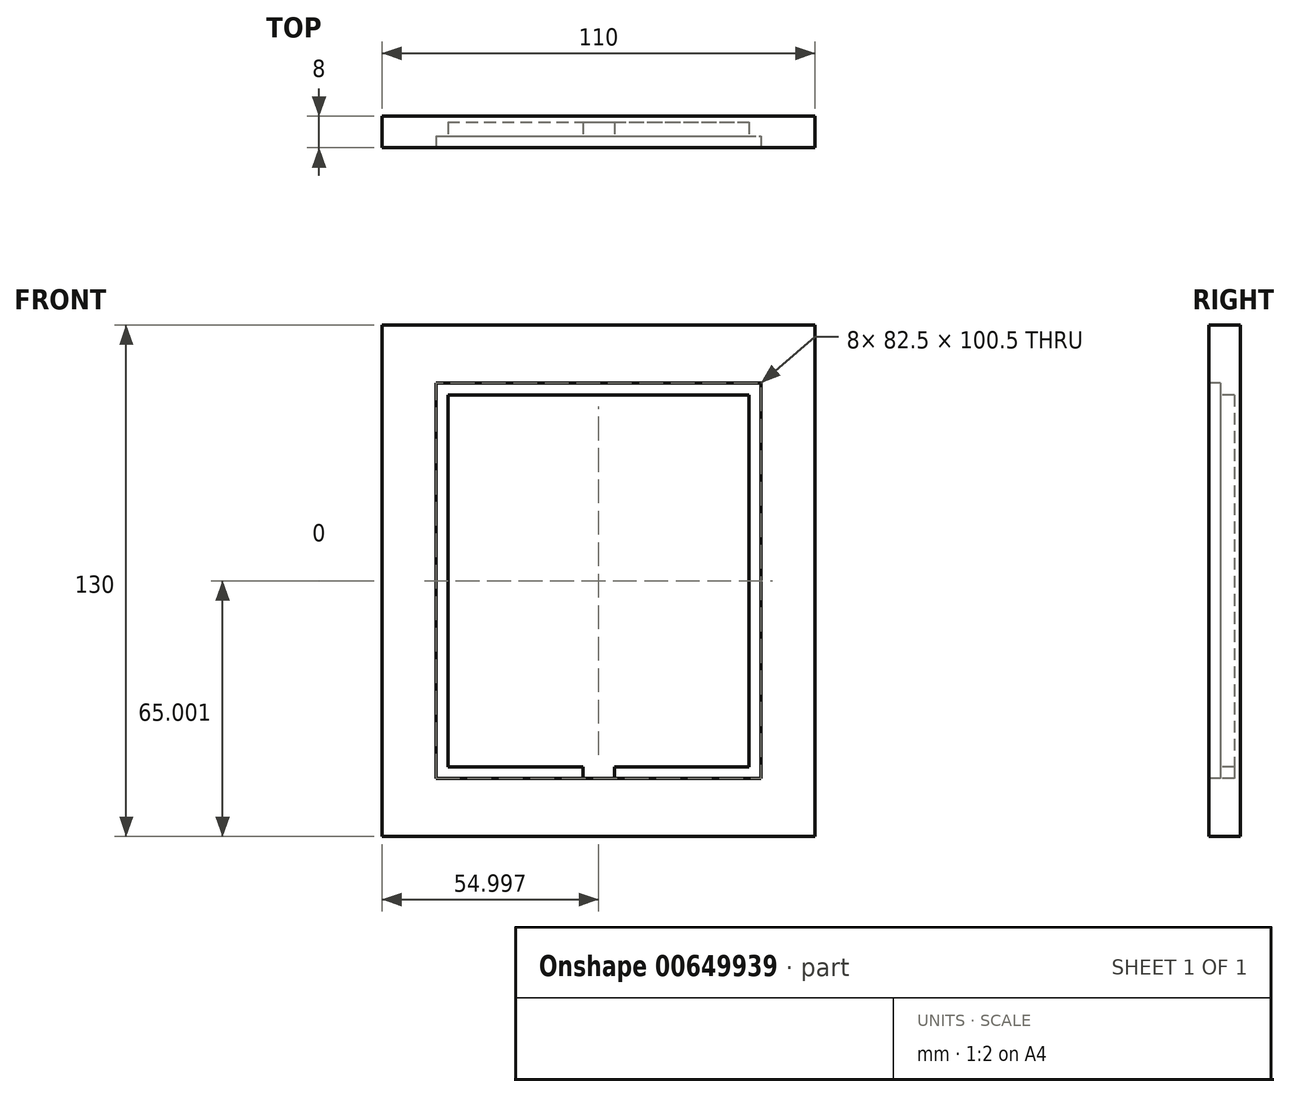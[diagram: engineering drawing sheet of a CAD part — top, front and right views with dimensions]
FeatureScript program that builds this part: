
annotation { "Feature Type Name" : "Feature", "Feature Type Description" : "" }
export const myFeature = defineFeature(function(context is Context, id is Id, definition is map)
    precondition{}
    {
        {
            var Q0;
            Q0=qCreatedBy(makeId("Front.planeOp"),FACE);
            var sketch = newSketch(context, id + "F0", { "sketchPlane" : qUnion([Q0])});
            skLineSegment(sketch, "E0.bottom", {"start": v(-59.1, 67.21) * mm, "end": v(50.9, 67.21) * mm});
            skLineSegment(sketch, "E0.top", {"start": v(-59.1, -62.79) * mm, "end": v(50.9, -62.79) * mm});
            skLineSegment(sketch, "E0.left", {"start": v(-59.1, 67.21) * mm, "end": v(-59.1, -62.79) * mm});
            skLineSegment(sketch, "E0.right", {"start": v(50.9, 67.21) * mm, "end": v(50.9, -62.79) * mm});
            skSolve(sketch);
        }
        {
            var Q0;
            Q0 = qSketchRegion(id + "F0", true);
            extrude(context, id + "F1", {"entities" : qUnion([Q0]), "depth" : 8 * mm, "offsetDistance" : 25 * mm});
        }
        {
            var Q0;
            Q0=makeQuery(id+"F1.opExtrude","CAP_FACE",FACE,{"disambiguationData":[OSD([sQuery(id+"F0.wireOp",EDGE,"E0.bottom"),sQuery(id+"F0.wireOp",EDGE,"E0.top"),sQuery(id+"F0.wireOp",EDGE,"E0.left"),sQuery(id+"F0.wireOp",EDGE,"E0.right")])],"isStart":false});
            var sketch = newSketch(context, id + "F2", { "sketchPlane" : qUnion([Q0])});
            skLineSegment(sketch, "E1.bottom", {"start": v(-45.34, 52.46) * mm, "end": v(37.16, 52.46) * mm});
            skLineSegment(sketch, "E1.top", {"start": v(-45.34, -48.04) * mm, "end": v(37.16, -48.04) * mm});
            skLineSegment(sketch, "E1.left", {"start": v(-45.34, 52.46) * mm, "end": v(-45.34, -48.04) * mm});
            skLineSegment(sketch, "E1.right", {"start": v(37.16, 52.46) * mm, "end": v(37.16, -48.04) * mm});
            skSolve(sketch);
        }
        {
            var Q0;
            Q0 = qSketchRegion(id + "F2", true);
            extrude(context, id + "F3", {"entities" : qUnion([Q0]), "operationType" : NewBodyOperationType.REMOVE, "oppositeDirection" : true, "depth" : 3 * mm, "offsetDistance" : 25 * mm});
        }
        {
            var Q0;
            Q0=makeQuery(id+"F3.boolean.opBoolean","COPY",FACE,{"derivedFrom":makeQuery(id+"F3.opExtrude","CAP_FACE",FACE,{"disambiguationData":[OSD([sQuery(id+"F2.wireOp",EDGE,"E1.bottom"),sQuery(id+"F2.wireOp",EDGE,"E1.top"),sQuery(id+"F2.wireOp",EDGE,"E1.left"),sQuery(id+"F2.wireOp",EDGE,"E1.right")])],"isStart":false})});
            var sketch = newSketch(context, id + "F4", { "sketchPlane" : qUnion([Q0])});
            skLineSegment(sketch, "E2.bottom", {"start": v(-42.34, 49.46) * mm, "end": v(34.16, 49.46) * mm});
            skLineSegment(sketch, "E2.top", {"start": v(-42.34, -45.04) * mm, "end": v(34.16, -45.04) * mm});
            skLineSegment(sketch, "E2.left", {"start": v(-42.34, 49.46) * mm, "end": v(-42.34, -45.04) * mm});
            skLineSegment(sketch, "E2.right", {"start": v(34.16, 49.46) * mm, "end": v(34.16, -45.04) * mm});
            skLineSegment(sketch, "E3.bottom", {"start": v(-8.1, -45.04) * mm, "end": v(-0.1, -45.04) * mm});
            skLineSegment(sketch, "E3.top", {"start": v(-8.1, -48.04) * mm, "end": v(-0.1, -48.04) * mm});
            skLineSegment(sketch, "E3.left", {"start": v(-8.1, -45.04) * mm, "end": v(-8.1, -48.04) * mm});
            skLineSegment(sketch, "E3.right", {"start": v(-0.1, -45.04) * mm, "end": v(-0.1, -48.04) * mm});
            skSolve(sketch);
        }
        {
            var Q0;
            Q0 = qSketchRegion(id + "F4", true);
            extrude(context, id + "F5", {"entities" : qUnion([Q0]), "operationType" : NewBodyOperationType.REMOVE, "oppositeDirection" : true, "depth" : 3.5 * mm, "offsetDistance" : 25 * mm});
        }
    });
